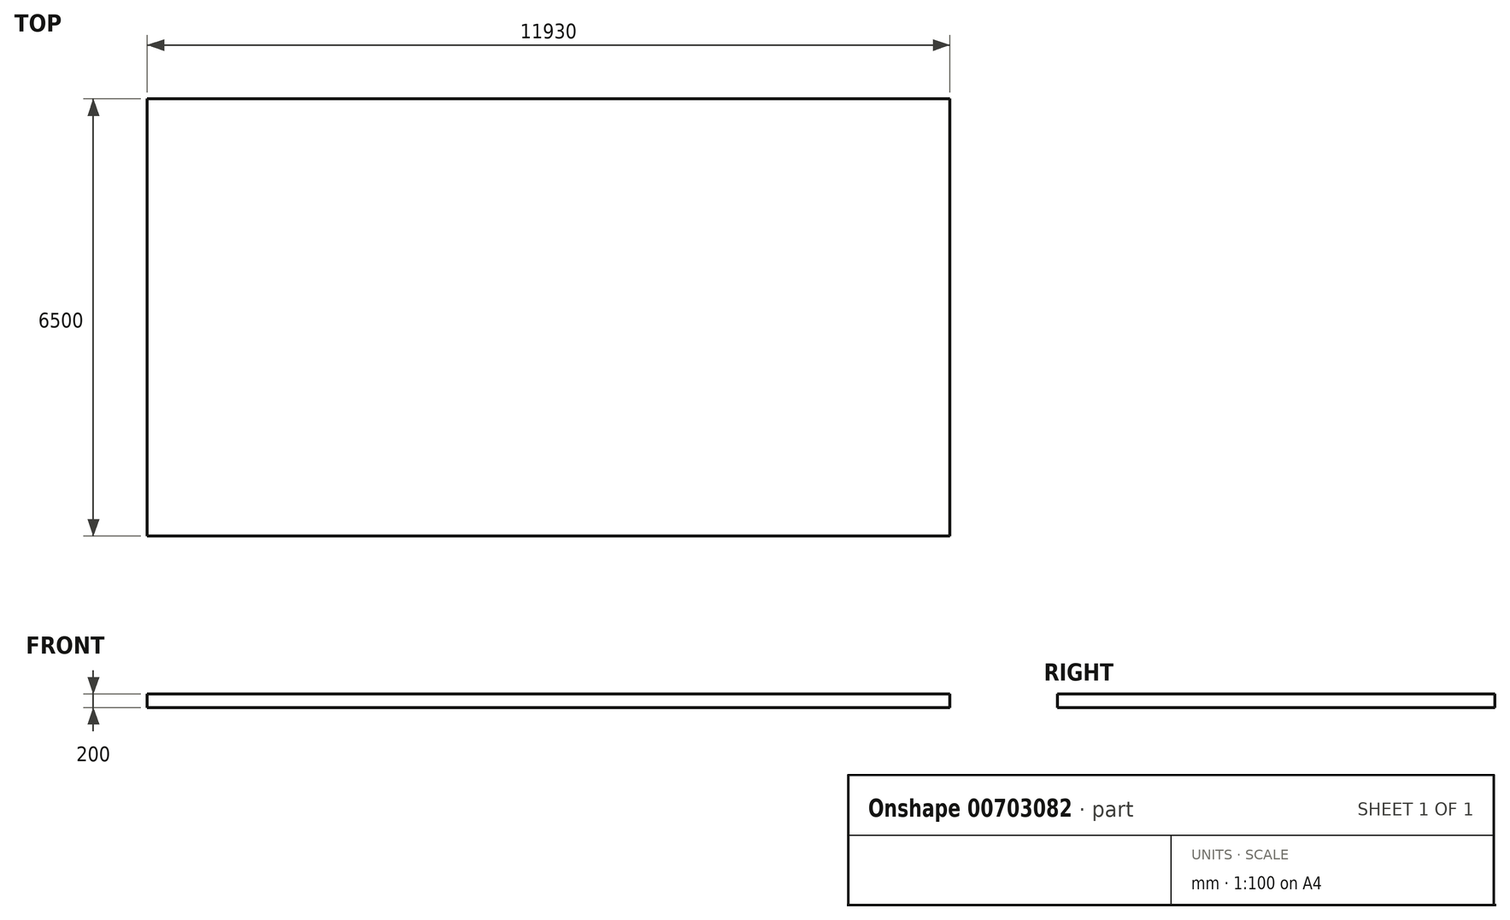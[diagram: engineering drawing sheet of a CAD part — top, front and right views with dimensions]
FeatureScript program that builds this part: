
annotation { "Feature Type Name" : "Feature", "Feature Type Description" : "" }
export const myFeature = defineFeature(function(context is Context, id is Id, definition is map)
    precondition{}
    {
        {
            var Q0;
            Q0=qCreatedBy(makeId("Top.planeOp"),FACE);
            var sketch = newSketch(context, id + "F0", { "sketchPlane" : qUnion([Q0])});
            skLineSegment(sketch, "E0.bottom", {"start": v(-5974.1, -5411.52) * mm, "end": v(5955.9, -5411.52) * mm});
            skLineSegment(sketch, "E0.top", {"start": v(-5974.1, 1088.48) * mm, "end": v(5955.9, 1088.48) * mm});
            skLineSegment(sketch, "E0.left", {"start": v(-5974.1, -5411.52) * mm, "end": v(-5974.1, 1088.48) * mm});
            skLineSegment(sketch, "E0.right", {"start": v(5955.9, -5411.52) * mm, "end": v(5955.9, 1088.48) * mm});
            skSolve(sketch);
        }
        {
            var Q0;
            Q0=makeQuery(id+"F0.imprint","IMPRINT",FACE,{"disambiguationData":[TD([[makeQuery(id+"F0.imprint","IMPRINT",EDGE,{"derivedFrom":sQuery(id+"F0.wireOp",EDGE,"E0.bottom")}),1.0]])]});
            extrude(context, id + "F1", {"entities" : qUnion([Q0]), "depth" : 200 * mm, "offsetDistance" : 25 * mm});
        }
    });
